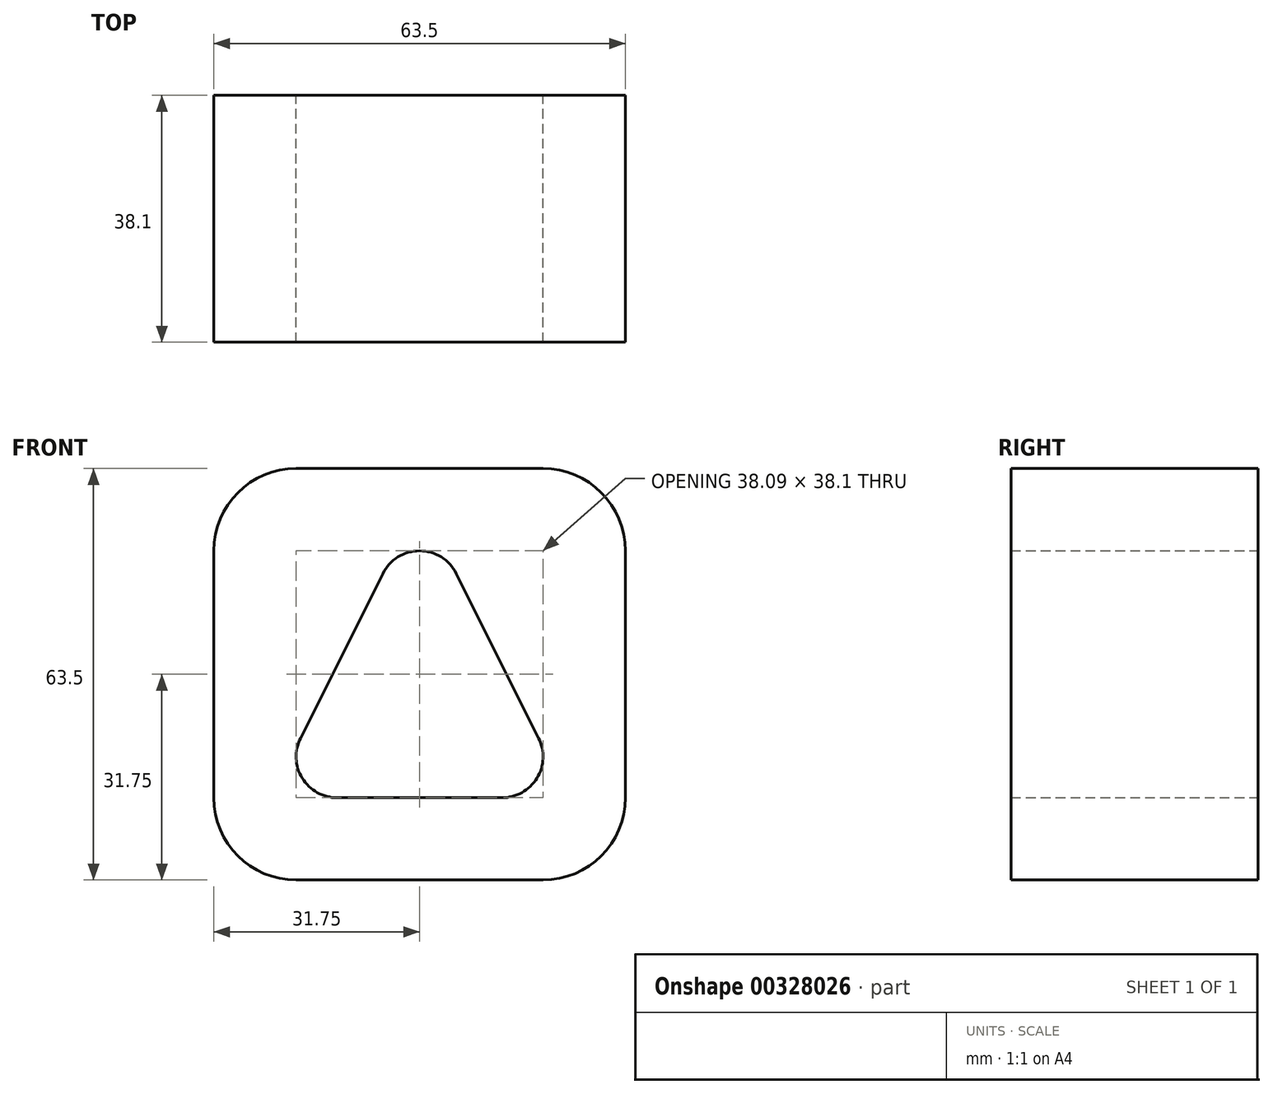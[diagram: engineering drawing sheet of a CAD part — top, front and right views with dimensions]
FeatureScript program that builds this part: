
annotation { "Feature Type Name" : "Feature", "Feature Type Description" : "" }
export const myFeature = defineFeature(function(context is Context, id is Id, definition is map)
    precondition{}
    {
        {
            var Q0;
            Q0=qCreatedBy(makeId("Front.planeOp"),FACE);
            var sketch = newSketch(context, id + "F0", { "sketchPlane" : qUnion([Q0])});
            skLineSegment(sketch, "E0.bottom", {"start": v(0, 63.5) * mm, "end": v(63.5, 63.5) * mm});
            skLineSegment(sketch, "E0.top", {"start": v(0, 0) * mm, "end": v(63.5, 0) * mm});
            skLineSegment(sketch, "E0.left", {"start": v(0, 63.5) * mm, "end": v(0, 0) * mm});
            skLineSegment(sketch, "E0.right", {"start": v(63.5, 63.5) * mm, "end": v(63.5, 0) * mm});
            skArc(sketch, "E1", {"start": v(13.37, 21.89) * mm, "mid": v(13.65, 15.71) * mm, "end": v(19.05, 12.7) * mm});
            skArc(sketch, "E2", {"start": v(37.43, 47.29) * mm, "mid": v(31.75, 50.8) * mm, "end": v(26.07, 47.29) * mm});
            skArc(sketch, "E3", {"start": v(44.45, 12.7) * mm, "mid": v(49.85, 15.71) * mm, "end": v(50.13, 21.89) * mm});
            skLineSegment(sketch, "E4", {"start": v(37.43, 47.29) * mm, "end": v(50.13, 21.89) * mm});
            skLineSegment(sketch, "E5", {"start": v(44.45, 12.7) * mm, "end": v(19.05, 12.7) * mm});
            skLineSegment(sketch, "E6", {"start": v(26.07, 47.29) * mm, "end": v(13.37, 21.89) * mm});
            skSolve(sketch);
        }
        {
            var Q0;
            Q0=makeQuery(id+"F0.imprint","IMPRINT",FACE,{"disambiguationData":[TD([[makeQuery(id+"F0.imprint","IMPRINT",EDGE,{"derivedFrom":sQuery(id+"F0.wireOp",EDGE,"E0.bottom")}),-1.0]])]});
            extrude(context, id + "F1", {"entities" : qUnion([Q0]), "depth" : 38.1 * mm});
        }
        {
            var Q0;
            Q0=makeQuery(id+"F1.opExtrude","SWEPT_EDGE",EDGE,{"disambiguationData":[OSD([sQuery(id+"F0.wireOp",EDGE,"E0.top"),sQuery(id+"F0.wireOp",EDGE,"E0.right")])]});
            var Q1;
            Q1=makeQuery(id+"F1.opExtrude","SWEPT_EDGE",EDGE,{"disambiguationData":[OSD([sQuery(id+"F0.wireOp",EDGE,"E0.bottom"),sQuery(id+"F0.wireOp",EDGE,"E0.right")])]});
            var Q2;
            Q2=makeQuery(id+"F1.opExtrude","SWEPT_EDGE",EDGE,{"disambiguationData":[OSD([sQuery(id+"F0.wireOp",EDGE,"E0.bottom"),sQuery(id+"F0.wireOp",EDGE,"E0.left")])]});
            var Q3;
            Q3=makeQuery(id+"F1.opExtrude","SWEPT_EDGE",EDGE,{"disambiguationData":[OSD([sQuery(id+"F0.wireOp",EDGE,"E0.top"),sQuery(id+"F0.wireOp",EDGE,"E0.left")])]});
            fillet(context, id + "F2", {"entities" : qUnion([Q0, Q1, Q2, Q3]), "radius" : 12.7 * mm, "tangentPropagation" : true, "allowEdgeOverflow" : false});
        }
    });
